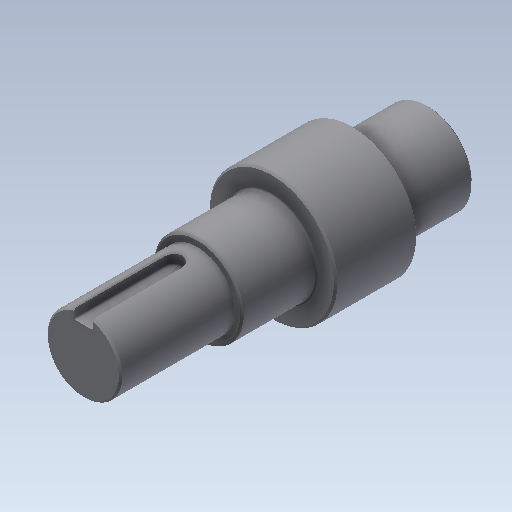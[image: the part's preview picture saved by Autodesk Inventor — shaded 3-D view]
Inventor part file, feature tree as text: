
AUTODESK INVENTOR PART (.ipt)
format: ipt  version: 2021 (Build 250183000, 183)  size: 235,520 bytes
history: native  units: in
note: dims shown in document units (in); Inventor stores cm internally (conversion verified against a paired STEP export)
features: other x11, sketch x5, extrude x4, fillet x1, revolve x1, chamfer x1
ambient origin geometry x8: Origin, YZ Plane, XZ Plane, XY Plane, X Axis, Y Axis, Z Axis, Center Point
bodies: Solid1 (feature_tree)
feature tree (23):
  extrude  "Extrusion1"  Depth=1.9063in
  extrude  "Extrusion2"  Depth=1.25in
  extrude  "Extrusion4"  Depth=1.074in
  fillet  "Fillet1"  Radius=0.06in
  extrude  "Extrusion3"  Depth=0.625in
  revolve  "Revolution1"  [1 undecoded]
  chamfer  "Chamfer1"  Distance=0.03in Angle=45.0deg
  other  "WP_H"
  other  "Centre1"
  other  "WP_End"
  other  "WP_K1"
  other  "WP_K2"
  other  "WP_L1"
  other  "WP_L3"
  other  "WP_M1"
  other  "WP_M2"
  other  "WP_N"
  other  "WP_O"
  sketch  "Sketch1"  dims[d0=1.25in d1=1.9063in]
  sketch  "Sketch2"  dims[d2=0.0in d3=1.25in]
  sketch  "Sketch3"  dims[d4=0.1555in d5=1.074in d6=0.06in]
  sketch  "Sketch4"  dims[d7=0.625in d8=0.625in]
  sketch  "Sketch5"  dims[d9=1.5in d10=0.0in d11=0.03in d12=0.125in d13=45.0deg d14=0.0in d16=3.875in d17=0.0in d19=1.07in d20=3.875in d21=0.7495in d22=1.375in d23=1.25in d24=0.7495in d25=0.03in d26=0.03in d27=0.03in d28=0.03in d29=0.03in d30=0.03in d31=0.03in d32=0.03in d33=0.03in d34=0.03in d35=90.0deg d36=1.0in d37=0.0in d38=0.03in]
note: 1 required parameter value undecoded (feature->parameter linkage not recoverable at this tier; creation-order binding heuristic only, values carry confidence <= 0.55)
